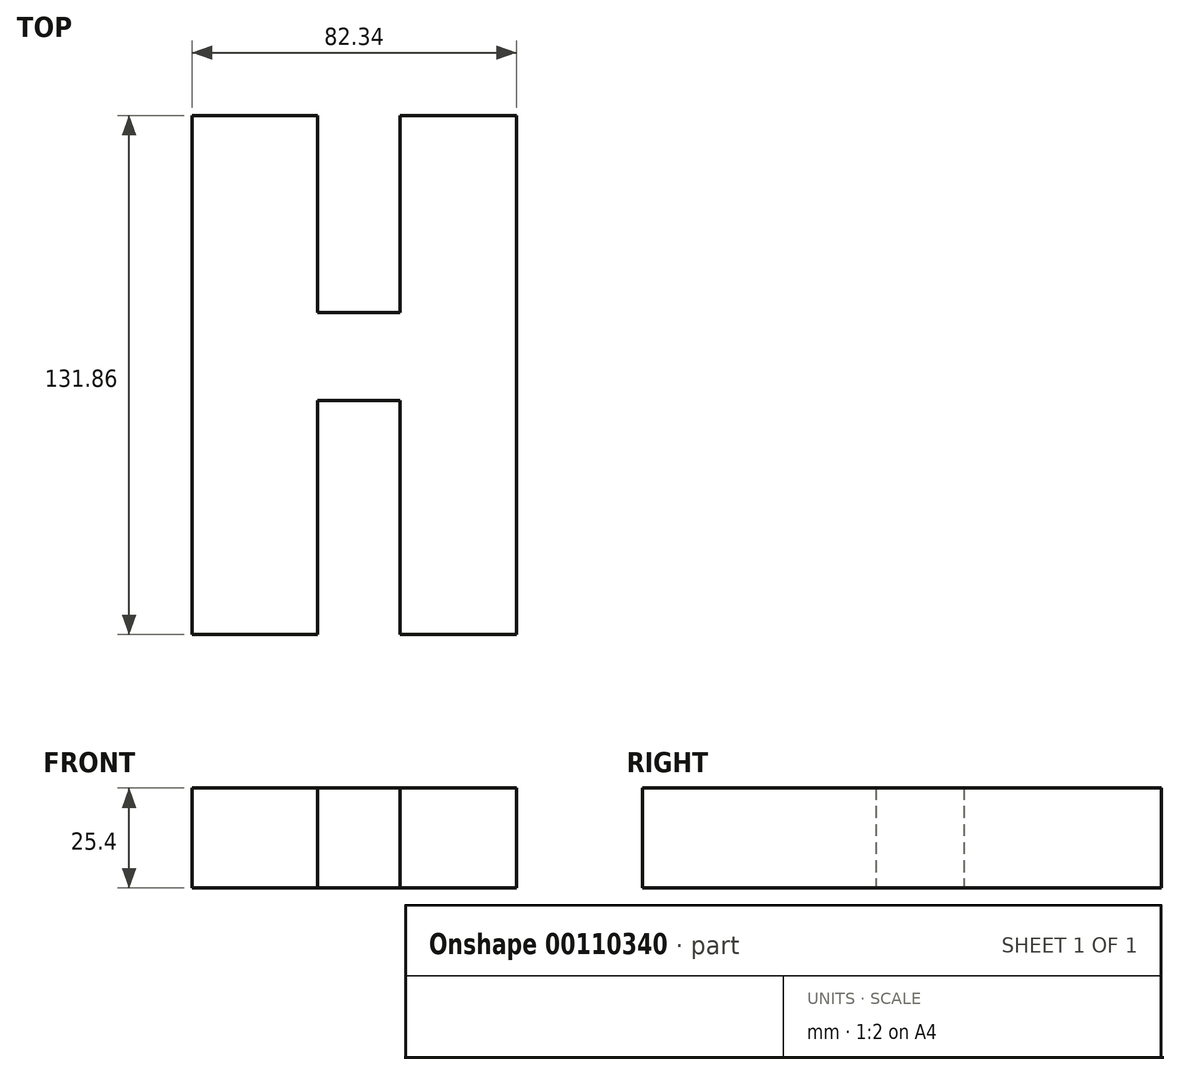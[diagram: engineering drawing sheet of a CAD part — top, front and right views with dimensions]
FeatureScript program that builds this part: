
annotation { "Feature Type Name" : "Feature", "Feature Type Description" : "" }
export const myFeature = defineFeature(function(context is Context, id is Id, definition is map)
    precondition{}
    {
        {
            var Q0;
            Q0=qCreatedBy(makeId("Top.planeOp"),FACE);
            var sketch = newSketch(context, id + "F0", { "sketchPlane" : qUnion([Q0])});
            skLineSegment(sketch, "E0.bottom", {"start": v(-63.11, 63.11) * mm, "end": v(-31.27, 63.11) * mm});
            skLineSegment(sketch, "E0.top", {"start": v(-63.11, -68.75) * mm, "end": v(-31.27, -68.75) * mm});
            skLineSegment(sketch, "E0.left", {"start": v(-63.11, 63.11) * mm, "end": v(-63.11, -68.75) * mm});
            skLineSegment(sketch, "E0.right", {"start": v(19.23, 63.11) * mm, "end": v(19.23, -68.75) * mm});
            skLineSegment(sketch, "E1.left", {"start": v(-31.27, 63.5) * mm, "end": v(-31.27, 13.01) * mm});
            skLineSegment(sketch, "E1.right", {"start": v(-10.3, 63.5) * mm, "end": v(-10.3, 13.01) * mm});
            skLineSegment(sketch, "E2.bottom", {"start": v(-31.27, 13.01) * mm, "end": v(-10.3, 13.01) * mm});
            skLineSegment(sketch, "E2.top", {"start": v(-31.27, -9.32) * mm, "end": v(-10.3, -9.32) * mm});
            skLineSegment(sketch, "E3.trimOffspring", {"start": v(-10.3, 63.11) * mm, "end": v(19.23, 63.11) * mm});
            skLineSegment(sketch, "E4.trimOffspring", {"start": v(-10.3, -9.32) * mm, "end": v(-10.3, -68.16) * mm});
            skLineSegment(sketch, "E5.trimOffspring", {"start": v(-31.27, -9.32) * mm, "end": v(-31.27, -68.16) * mm});
            skLineSegment(sketch, "E6.left", {"start": v(-31.27, -9.32) * mm, "end": v(-31.27, -68.75) * mm});
            skLineSegment(sketch, "E6.right", {"start": v(-10.3, -9.32) * mm, "end": v(-10.3, -68.75) * mm});
            skLineSegment(sketch, "E7.trimOffspring", {"start": v(-10.3, -68.75) * mm, "end": v(19.23, -68.75) * mm});
            skSolve(sketch);
        }
        {
            var Q0;
            {var subQ1=sQuery(id+"F0.wireOp",EDGE,"E0.bottom");Q0=makeQuery(id+"F0.imprint","IMPRINT",FACE,{"disambiguationData":[TD([[makeQuery(id+"F0.imprint","IMPRINT",EDGE,{"derivedFrom":subQ1}),-1.0]])]});}
            extrude(context, id + "F1", {"entities" : qUnion([Q0]), "depth" : 25.4 * mm});
        }
    });
